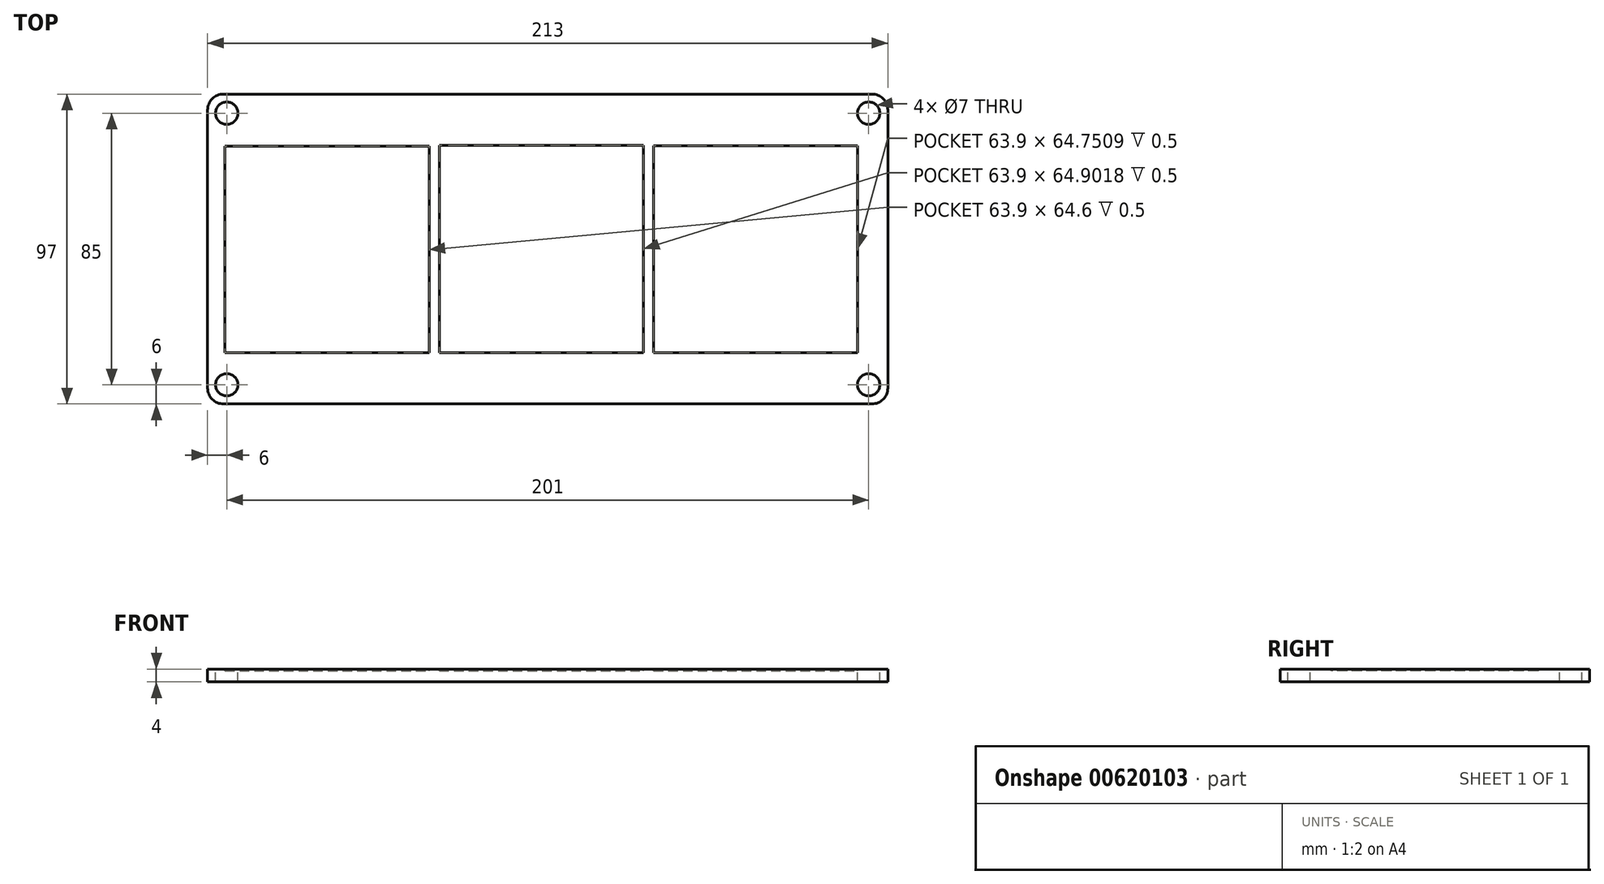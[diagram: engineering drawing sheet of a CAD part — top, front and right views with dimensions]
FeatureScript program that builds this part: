
annotation { "Feature Type Name" : "Feature", "Feature Type Description" : "" }
export const myFeature = defineFeature(function(context is Context, id is Id, definition is map)
    precondition{}
    {
        {
            var Q0;
            Q0=qCreatedBy(makeId("Top.planeOp"),FACE);
            var sketch = newSketch(context, id + "F0", { "sketchPlane" : qUnion([Q0])});
            skLineSegment(sketch, "E0.bottom", {"start": v(101.5, -48.5) * mm, "end": v(-101.5, -48.5) * mm});
            skLineSegment(sketch, "E0.top", {"start": v(101.5, 48.5) * mm, "end": v(-101.5, 48.5) * mm});
            skLineSegment(sketch, "E0.left", {"start": v(106.5, -43.5) * mm, "end": v(106.5, 43.5) * mm});
            skLineSegment(sketch, "E0.right", {"start": v(-106.5, -43.5) * mm, "end": v(-106.5, 43.5) * mm});
            skPoint(sketch, "E0.middle", {"position": v(0, 0) * mm});
            skCircle(sketch, "E1", {"center": v(-100.5, 42.5) * mm, "radius": 3.5 * mm});
            skCircle(sketch, "E2", {"center": v(-100.5, -42.5) * mm, "radius": 3.5 * mm});
            skCircle(sketch, "E3", {"center": v(100.5, 42.5) * mm, "radius": 3.5 * mm});
            skCircle(sketch, "E4", {"center": v(100.5, -42.5) * mm, "radius": 3.5 * mm});
            skPoint(sketch, "E5.visualSharp", {"position": v(-106.5, 48.5) * mm});
            skArc(sketch, "E5.filletArc", {"start": v(-101.5, 48.5) * mm, "mid": v(-105.04, 47.04) * mm, "end": v(-106.5, 43.5) * mm});
            skPoint(sketch, "E6.visualSharp", {"position": v(106.5, 48.5) * mm});
            skArc(sketch, "E6.filletArc", {"start": v(106.5, 43.5) * mm, "mid": v(105.04, 47.04) * mm, "end": v(101.5, 48.5) * mm});
            skPoint(sketch, "E7.visualSharp", {"position": v(106.5, -48.5) * mm});
            skArc(sketch, "E7.filletArc", {"start": v(101.5, -48.5) * mm, "mid": v(105.04, -47.04) * mm, "end": v(106.5, -43.5) * mm});
            skPoint(sketch, "E8.visualSharp", {"position": v(-106.5, -48.5) * mm});
            skArc(sketch, "E8.filletArc", {"start": v(-106.5, -43.5) * mm, "mid": v(-105.04, -47.04) * mm, "end": v(-101.5, -48.5) * mm});
            skSolve(sketch);
        }
        {
            var Q0;
            Q0=makeQuery(id+"F0.imprint","IMPRINT",FACE,{"disambiguationData":[TD([[makeQuery(id+"F0.imprint","IMPRINT",EDGE,{"derivedFrom":sQuery(id+"F0.wireOp",EDGE,"E0.bottom")}),-1.0]])]});
            var sketch = newSketch(context, id + "F1", { "sketchPlane" : qUnion([Q0])});
            skLineSegment(sketch, "E9.bottom", {"start": v(-101.05, 32.15) * mm, "end": v(-37.15, 32.15) * mm});
            skLineSegment(sketch, "E9.top", {"start": v(-101.05, -32.45) * mm, "end": v(-37.15, -32.45) * mm});
            skLineSegment(sketch, "E9.left", {"start": v(-101.05, 32.15) * mm, "end": v(-101.05, -32.45) * mm});
            skLineSegment(sketch, "E9.right", {"start": v(-37.15, 32.15) * mm, "end": v(-37.15, -32.45) * mm});
            skLineSegment(sketch, "E10.bottom", {"start": v(-33.95, 32.45) * mm, "end": v(29.95, 32.45) * mm});
            skLineSegment(sketch, "E10.top", {"start": v(-33.95, -32.45) * mm, "end": v(29.95, -32.45) * mm});
            skLineSegment(sketch, "E10.left", {"start": v(-33.95, 32.45) * mm, "end": v(-33.95, -32.45) * mm});
            skLineSegment(sketch, "E10.right", {"start": v(29.95, 32.45) * mm, "end": v(29.95, -32.45) * mm});
            skLineSegment(sketch, "E11.bottom", {"start": v(33.15, 32.3) * mm, "end": v(97.05, 32.3) * mm});
            skLineSegment(sketch, "E11.top", {"start": v(33.15, -32.45) * mm, "end": v(97.05, -32.45) * mm});
            skLineSegment(sketch, "E11.left", {"start": v(33.15, 32.3) * mm, "end": v(33.15, -32.45) * mm});
            skLineSegment(sketch, "E11.right", {"start": v(97.05, 32.3) * mm, "end": v(97.05, -32.45) * mm});
            skSolve(sketch);
        }
        {
            var Q0;
            Q0 = qSketchRegion(id + "F0", true);
            var Q1;
            Q1=makeQuery(id+"F0.imprint","IMPRINT",FACE,{"disambiguationData":[TD([[makeQuery(id+"F0.imprint","IMPRINT",EDGE,{"derivedFrom":sQuery(id+"F0.wireOp",EDGE,"E0.bottom")}),-1.0]])]});
            extrude(context, id + "F2", {"entities" : qUnion([Q0, Q1]), "oppositeDirection" : true, "depth" : 4 * mm, "offsetDistance" : 25 * mm});
        }
        {
            var Q0;
            Q0 = qSketchRegion(id + "F1", true);
            extrude(context, id + "F3", {"entities" : qUnion([Q0]), "operationType" : NewBodyOperationType.REMOVE, "oppositeDirection" : true, "depth" : 0.5 * mm, "offsetDistance" : 25 * mm});
        }
    });
